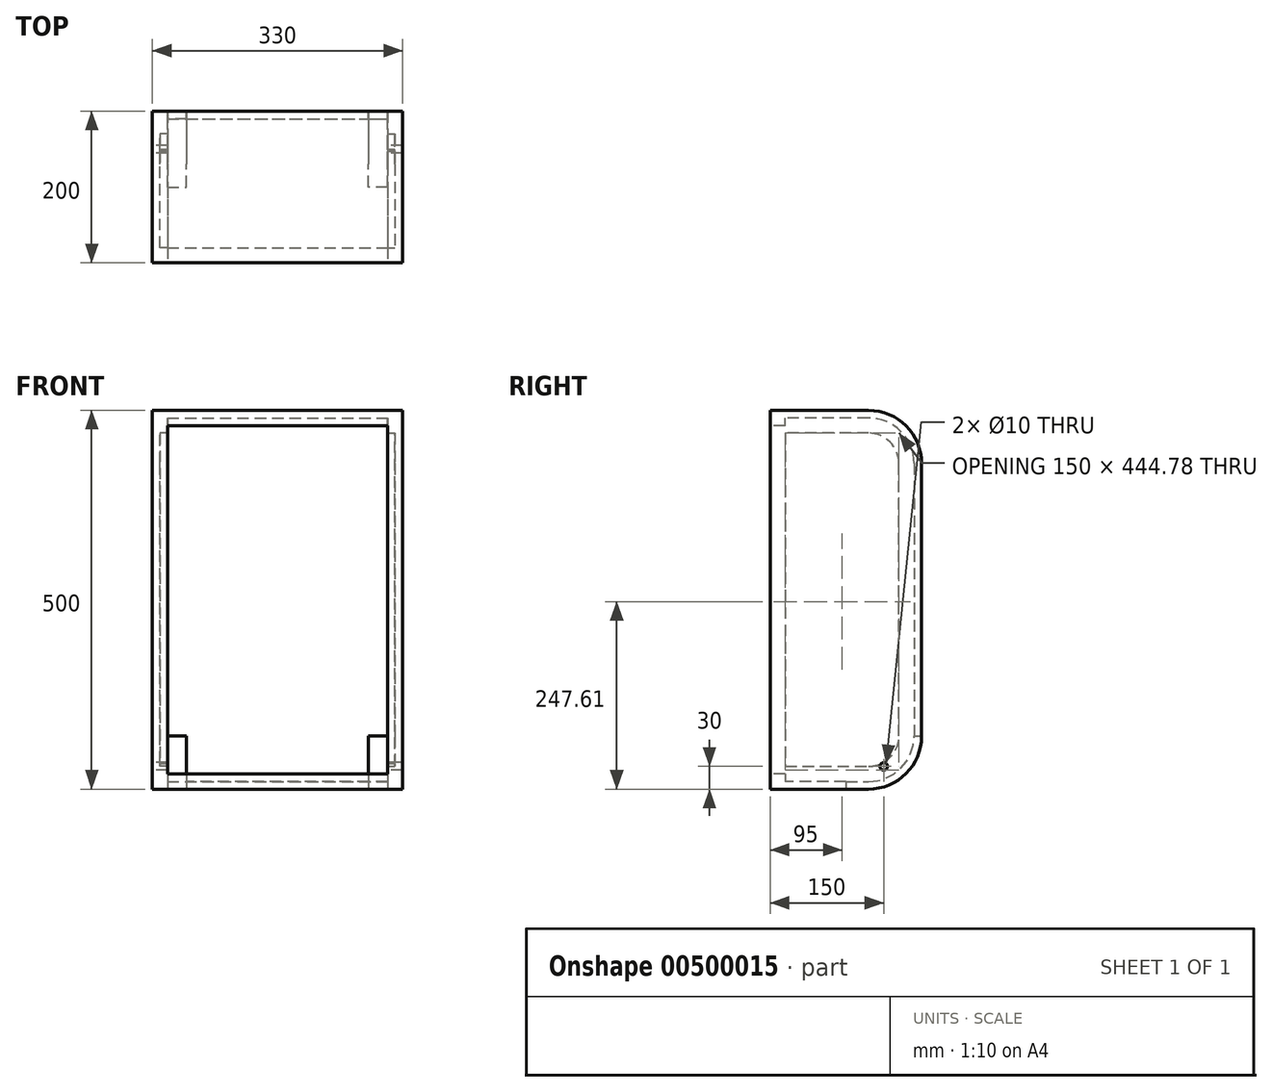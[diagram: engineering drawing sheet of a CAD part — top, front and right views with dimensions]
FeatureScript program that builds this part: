
annotation { "Feature Type Name" : "Feature", "Feature Type Description" : "" }
export const myFeature = defineFeature(function(context is Context, id is Id, definition is map)
    precondition{}
    {
        {
            var Q0;
            Q0=qCreatedBy(makeId("Front.planeOp"),FACE);
            var sketch = newSketch(context, id + "F0", { "sketchPlane" : qUnion([Q0])});
            skLineSegment(sketch, "E0.bottom", {"start": v(0, 0) * mm, "end": v(330, 0) * mm});
            skLineSegment(sketch, "E0.top", {"start": v(0, -500) * mm, "end": v(330, -500) * mm});
            skLineSegment(sketch, "E0.left", {"start": v(0, 0) * mm, "end": v(0, -500) * mm});
            skLineSegment(sketch, "E0.right", {"start": v(330, 0) * mm, "end": v(330, -500) * mm});
            skSolve(sketch);
        }
        {
            var Q0;
            Q0 = qSketchRegion(id + "F0", true);
            extrude(context, id + "F1", {"entities" : qUnion([Q0]), "oppositeDirection" : true, "depth" : 200 * mm});
        }
        {
            var Q0;
            Q0=makeQuery(id+"F1.opExtrude","CAP_EDGE",EDGE,{"disambiguationData":[OSD([sQuery(id+"F0.wireOp",EDGE,"E0.bottom")])],"isStart":false});
            var Q1;
            Q1=makeQuery(id+"F1.opExtrude","CAP_EDGE",EDGE,{"disambiguationData":[OSD([sQuery(id+"F0.wireOp",EDGE,"E0.top")])],"isStart":false});
            fillet(context, id + "F2", {"entities" : qUnion([Q0, Q1]), "radius" : 70 * mm, "tangentPropagation" : true, "allowEdgeOverflow" : false});
        }
        {
            var Q0;
            Q0=makeQuery(id+"F1.opExtrude","CAP_FACE",FACE,{"disambiguationData":[OSD([sQuery(id+"F0.wireOp",EDGE,"E0.bottom"),sQuery(id+"F0.wireOp",EDGE,"E0.top"),sQuery(id+"F0.wireOp",EDGE,"E0.left"),sQuery(id+"F0.wireOp",EDGE,"E0.right")])],"isStart":true});
            shell(context, id + "F3", {"entities" : qUnion([Q0]), "thickness" : 10 * mm});
        }
        {
            var Q0;
            Q0=makeQuery(id+"F3.opShell","OFFSET_FACE",FACE,{"disambiguationData":[OSD([sQuery(id+"F0.wireOp",EDGE,"E0.left")])]});
            var sketch = newSketch(context, id + "F4", { "sketchPlane" : qUnion([Q0])});
            skArc(sketch, "E1.0", {"start": v(130, -470) * mm, "mid": v(158.28, -458.28) * mm, "end": v(170, -430) * mm});
            skArc(sketch, "E1.1", {"start": v(170, -70) * mm, "mid": v(158.28, -41.72) * mm, "end": v(130, -30) * mm});
            skLineSegment(sketch, "E1.2", {"start": v(130, -30) * mm, "end": v(20, -30) * mm});
            skLineSegment(sketch, "E1.3", {"start": v(170, -430) * mm, "end": v(170, -70) * mm});
            skLineSegment(sketch, "E1.4", {"start": v(20, -30) * mm, "end": v(20, -470) * mm});
            skLineSegment(sketch, "E1.5", {"start": v(20, -470) * mm, "end": v(130, -470) * mm});
            skLineSegment(sketch, "E2.0", {"start": v(130, -10) * mm, "end": v(0, -10) * mm});
            skArc(sketch, "E2.1", {"start": v(130, -10) * mm, "mid": v(172.43, -27.57) * mm, "end": v(190, -70) * mm});
            skLineSegment(sketch, "E2.2", {"start": v(190, -70) * mm, "end": v(190, -430) * mm});
            skLineSegment(sketch, "E2.3", {"start": v(0, -10) * mm, "end": v(0, -490) * mm});
            skArc(sketch, "E3.0", {"start": v(190, -430) * mm, "mid": v(172.43, -472.43) * mm, "end": v(130, -490) * mm});
            skLineSegment(sketch, "E3.1", {"start": v(130, -490) * mm, "end": v(0, -490) * mm});
            skSolve(sketch);
        }
        {
            var Q0;
            Q0 = qSketchRegion(id + "F4", true);
            extrude(context, id + "F5", {"entities" : qUnion([Q0]), "operationType" : NewBodyOperationType.ADD, "depth" : 10 * mm});
        }
        {
            var Q0;
            Q0=makeQuery(id+"F3.opShell","OFFSET_FACE",FACE,{"disambiguationData":[OSD([sQuery(id+"F0.wireOp",EDGE,"E0.right")])]});
            var sketch = newSketch(context, id + "F6", { "sketchPlane" : qUnion([Q0])});
            skLineSegment(sketch, "E4.0", {"start": v(-130, -490) * mm, "end": v(0, -490) * mm});
            skLineSegment(sketch, "E4.1", {"start": v(0, -10) * mm, "end": v(0, -490) * mm});
            skArc(sketch, "E4.2", {"start": v(-130, -490) * mm, "mid": v(-172.43, -472.43) * mm, "end": v(-190, -430) * mm});
            skLineSegment(sketch, "E4.3", {"start": v(-190, -70) * mm, "end": v(-190, -430) * mm});
            skArc(sketch, "E5.0", {"start": v(-190, -70) * mm, "mid": v(-172.43, -27.57) * mm, "end": v(-130, -10) * mm});
            skLineSegment(sketch, "E5.1", {"start": v(-130, -10) * mm, "end": v(0, -10) * mm});
            skArc(sketch, "E6.0", {"start": v(-130, -470) * mm, "mid": v(-158.28, -458.28) * mm, "end": v(-170, -430) * mm});
            skLineSegment(sketch, "E6.1", {"start": v(-20, -470) * mm, "end": v(-20, -30) * mm});
            skLineSegment(sketch, "E6.2", {"start": v(-20, -30) * mm, "end": v(-130, -30) * mm});
            skLineSegment(sketch, "E6.3", {"start": v(-130, -470) * mm, "end": v(-20, -470) * mm});
            skArc(sketch, "E6.4", {"start": v(-170, -70) * mm, "mid": v(-158.28, -41.72) * mm, "end": v(-130, -30) * mm});
            skLineSegment(sketch, "E6.5", {"start": v(-170, -70) * mm, "end": v(-170, -430) * mm});
            skSolve(sketch);
        }
        {
            var Q0;
            Q0 = qSketchRegion(id + "F6", true);
            extrude(context, id + "F7", {"entities" : qUnion([Q0]), "operationType" : NewBodyOperationType.ADD, "depth" : 10 * mm});
        }
        {
            var Q0;
            {var subQ0=sQuery(id+"F0.wireOp",EDGE,"E0.top");Q0=makeQuery(id+"F3.opShell","OFFSET_FACE",FACE,{"disambiguationData":[OSD([subQ0]),TDD([makeQuery(id+"F1.opExtrude","SWEPT_FACE",FACE,{"disambiguationData":[OSD([subQ0])]})])]});}
            var sketch = newSketch(context, id + "F8", { "sketchPlane" : qUnion([Q0])});
            skLineSegment(sketch, "E7.bottom", {"start": v(20, 0) * mm, "end": v(310, 0) * mm});
            skLineSegment(sketch, "E7.top", {"start": v(20, 20) * mm, "end": v(310, 20) * mm});
            skLineSegment(sketch, "E7.left", {"start": v(20, 0) * mm, "end": v(20, 20) * mm});
            skLineSegment(sketch, "E7.right", {"start": v(310, 0) * mm, "end": v(310, 20) * mm});
            skSolve(sketch);
        }
        {
            var Q0;
            Q0 = qSketchRegion(id + "F8", true);
            extrude(context, id + "F9", {"entities" : qUnion([Q0]), "operationType" : NewBodyOperationType.ADD, "depth" : 10 * mm});
        }
        {
            var Q0;
            {var subQ0=sQuery(id+"F0.wireOp",EDGE,"E0.bottom");Q0=makeQuery(id+"F3.opShell","OFFSET_FACE",FACE,{"disambiguationData":[OSD([subQ0]),TDD([makeQuery(id+"F1.opExtrude","SWEPT_FACE",FACE,{"disambiguationData":[OSD([subQ0])]})])]});}
            var sketch = newSketch(context, id + "F10", { "sketchPlane" : qUnion([Q0])});
            skLineSegment(sketch, "E8.bottom", {"start": v(20, 0) * mm, "end": v(310, 0) * mm});
            skLineSegment(sketch, "E8.top", {"start": v(20, -20) * mm, "end": v(310, -20) * mm});
            skLineSegment(sketch, "E8.left", {"start": v(20, 0) * mm, "end": v(20, -20) * mm});
            skLineSegment(sketch, "E8.right", {"start": v(310, 0) * mm, "end": v(310, -20) * mm});
            skSolve(sketch);
        }
        {
            var Q0;
            Q0 = qSketchRegion(id + "F10", true);
            extrude(context, id + "F11", {"entities" : qUnion([Q0]), "operationType" : NewBodyOperationType.ADD, "depth" : 10 * mm});
        }
        {
            var Q0;
            Q0=makeQuery(id+"F1.opExtrude","SWEPT_FACE",FACE,{"disambiguationData":[OSD([sQuery(id+"F0.wireOp",EDGE,"E0.left")])]});
            var sketch = newSketch(context, id + "F12", { "sketchPlane" : qUnion([Q0])});
            skCircle(sketch, "E9", {"center": v(-150, -470) * mm, "radius": 50 * mm});
            skSolve(sketch);
        }
        {
            var Q0;
            Q0=makeQuery(id+"F1.opExtrude","SWEPT_FACE",FACE,{"disambiguationData":[OSD([sQuery(id+"F0.wireOp",EDGE,"E0.top")])]});
            var sketch = newSketch(context, id + "F13", { "sketchPlane" : qUnion([Q0])});
            skLineSegment(sketch, "E10.bottom", {"start": v(20, -100) * mm, "end": v(45, -100) * mm});
            skLineSegment(sketch, "E10.top", {"start": v(20, -200) * mm, "end": v(45, -200) * mm});
            skLineSegment(sketch, "E10.left", {"start": v(20, -100) * mm, "end": v(20, -200) * mm});
            skLineSegment(sketch, "E10.right", {"start": v(45, -100) * mm, "end": v(45, -200) * mm});
            skLineSegment(sketch, "E11.bottom", {"start": v(310, -100) * mm, "end": v(285, -100) * mm});
            skLineSegment(sketch, "E11.top", {"start": v(310, -200) * mm, "end": v(285, -200) * mm});
            skLineSegment(sketch, "E11.left", {"start": v(310, -100) * mm, "end": v(310, -200) * mm});
            skLineSegment(sketch, "E11.right", {"start": v(285, -100) * mm, "end": v(285, -200) * mm});
            skSolve(sketch);
        }
        {
            var Q0;
            Q0 = qSketchRegion(id + "F13", true);
            extrude(context, id + "F14", {"entities" : qUnion([Q0]), "operationType" : NewBodyOperationType.REMOVE, "oppositeDirection" : true, "depth" : 70 * mm});
        }
        {
            var Q0;
            {var subQ0=sQuery(id+"F12.wireOp",EDGE,"E9");var subQ1=sQuery(id+"F0.wireOp",EDGE,"E0.left");var subQ2=sQuery(id+"F0.wireOp",EDGE,"E0.top");var subQ3=makeQuery(id+"F1.opExtrude","SWEPT_EDGE",EDGE,{"disambiguationData":[OSD([subQ2,subQ1])]});var subQ4=makeQuery(id+"F12.imprint","INTERSECT",VERTEX,{"derivedFrom":[subQ3,subQ0]});Q0=makeQuery(id+"F12.imprint","IMPRINT",FACE,{"disambiguationData":[TD([[makeQuery(id+"F12.imprint","IMPRINT",EDGE,{"disambiguationData":[TD([[subQ4,-1.0]])],"derivedFrom":subQ0}),1.0]])]});}
            var sketch = newSketch(context, id + "F15", { "sketchPlane" : qUnion([Q0])});
            skCircle(sketch, "E12", {"center": v(-150, -470) * mm, "radius": 5 * mm});
            skSolve(sketch);
        }
        {
            var Q0;
            Q0 = qSketchRegion(id + "F15", true);
            extrude(context, id + "F16", {"entities" : qUnion([Q0]), "operationType" : NewBodyOperationType.REMOVE, "endBound" : BoundingType.THROUGH_ALL, "oppositeDirection" : true, "depth" : 25 * mm});
        }
    });
